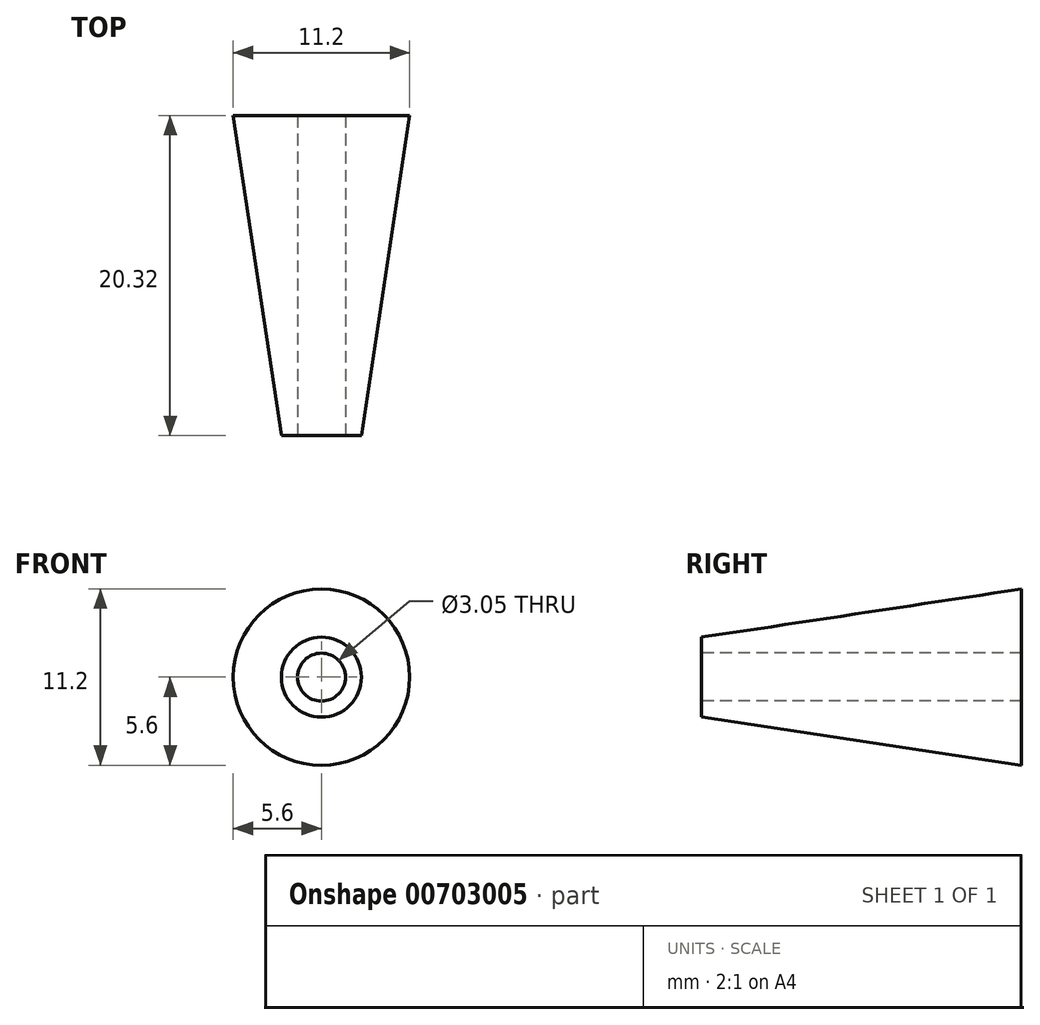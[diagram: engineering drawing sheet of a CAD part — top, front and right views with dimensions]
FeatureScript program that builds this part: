
annotation { "Feature Type Name" : "Feature", "Feature Type Description" : "" }
export const myFeature = defineFeature(function(context is Context, id is Id, definition is map)
    precondition{}
    {
        {
            var Q0;
            Q0=qCreatedBy(makeId("Right.planeOp"),FACE);
            var sketch = newSketch(context, id + "F0", { "sketchPlane" : qUnion([Q0])});
            skLineSegment(sketch, "E0", {"start": v(-61.85, 123.13) * mm, "end": v(-82.17, 123.13) * mm});
            skLineSegment(sketch, "E1", {"start": v(-82.17, 123.13) * mm, "end": v(-82.17, 120.59) * mm});
            skLineSegment(sketch, "E2", {"start": v(-82.17, 120.59) * mm, "end": v(-61.85, 117.53) * mm});
            skLineSegment(sketch, "E3", {"start": v(-61.85, 117.53) * mm, "end": v(-61.85, 123.13) * mm});
            skSolve(sketch);
        }
        {
            var Q0;
            Q0=makeQuery(id+"F0.imprint","IMPRINT",FACE,{"disambiguationData":[TD([[makeQuery(id+"F0.imprint","IMPRINT",EDGE,{"derivedFrom":sQuery(id+"F0.wireOp",EDGE,"E0")}),1.0]])]});
            var Q1;
            Q1=sQuery(id+"F0.wireOp",EDGE,"E0");
            revolve(context, id + "F1", {"surfaceOperationType" : NewSurfaceOperationType.NEW, "entities" : qUnion([Q0]), "axis" : qUnion([Q1]), "revolveType" : RevolveType.FULL});
        }
        {
            var Q0;
            Q0=makeQuery(id+"F1.opRevolve","SWEPT_FACE",FACE,{"disambiguationData":[OSD([sQuery(id+"F0.wireOp",EDGE,"E1")])]});
            var sketch = newSketch(context, id + "F2", { "sketchPlane" : qUnion([Q0])});
            skCircle(sketch, "E4", {"center": v(0, 123.13) * mm, "radius": 1.52 * mm});
            skSolve(sketch);
        }
        {
            var Q0;
            Q0=makeQuery(id+"F2.imprint","IMPRINT",FACE,{"disambiguationData":[TD([[makeQuery(id+"F2.imprint","IMPRINT",EDGE,{"derivedFrom":sQuery(id+"F2.wireOp",EDGE,"E4")}),1.0]])]});
            extrude(context, id + "F3", {"entities" : qUnion([Q0]), "operationType" : NewBodyOperationType.REMOVE, "oppositeDirection" : true, "depth" : 20.32 * mm, "offsetDistance" : 25.4 * mm});
        }
    });
